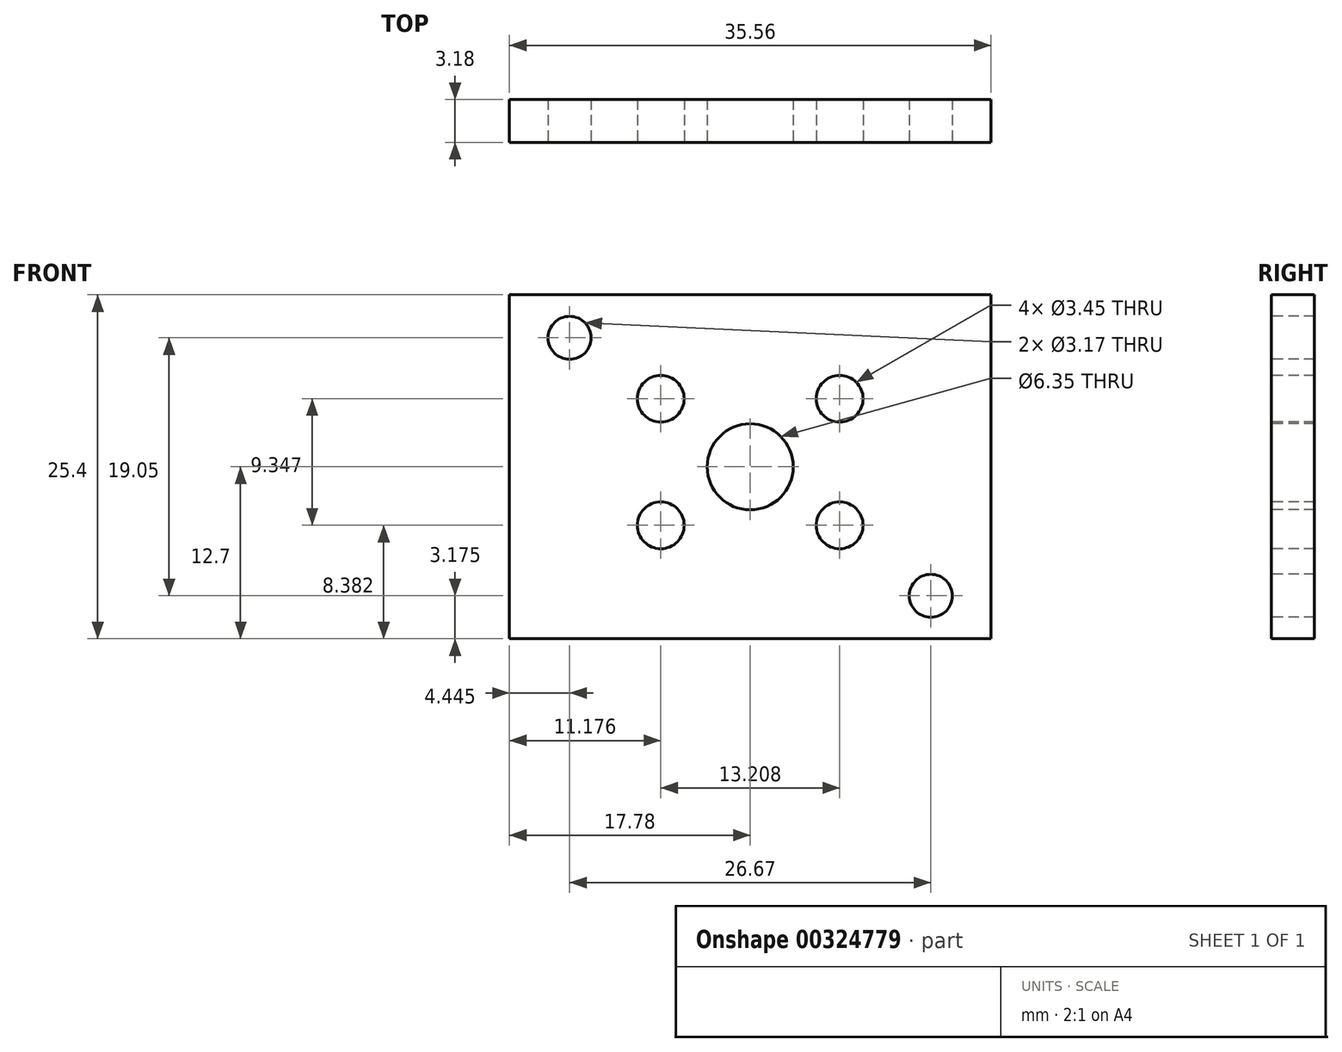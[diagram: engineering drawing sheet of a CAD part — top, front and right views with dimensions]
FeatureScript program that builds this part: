
annotation { "Feature Type Name" : "Feature", "Feature Type Description" : "" }
export const myFeature = defineFeature(function(context is Context, id is Id, definition is map)
    precondition{}
    {
        {
            var Q0;
            Q0=qCreatedBy(makeId("Front.planeOp"),FACE);
            var sketch = newSketch(context, id + "F0", { "sketchPlane" : qUnion([Q0])});
            skLineSegment(sketch, "E0.bottom", {"start": v(17.78, -12.7) * mm, "end": v(-17.78, -12.7) * mm});
            skLineSegment(sketch, "E0.top", {"start": v(17.78, 12.7) * mm, "end": v(-17.78, 12.7) * mm});
            skLineSegment(sketch, "E0.left", {"start": v(17.78, -12.7) * mm, "end": v(17.78, 12.7) * mm});
            skLineSegment(sketch, "E0.right", {"start": v(-17.78, -12.7) * mm, "end": v(-17.78, 12.7) * mm});
            skPoint(sketch, "E0.middle", {"position": v(0, 0) * mm});
            skSolve(sketch);
        }
        {
            var Q0;
            Q0=makeQuery(id+"F0.imprint","IMPRINT",FACE,{"disambiguationData":[TD([[makeQuery(id+"F0.imprint","IMPRINT",EDGE,{"derivedFrom":sQuery(id+"F0.wireOp",EDGE,"E0.bottom")}),-1.0]])]});
            extrude(context, id + "F1", {"entities" : qUnion([Q0]), "depth" : 3.17 * mm, "offsetDistance" : 25.4 * mm});
        }
        {
            var Q0;
            Q0=makeQuery(id+"F1.opExtrude","CAP_FACE",FACE,{"disambiguationData":[OSD([sQuery(id+"F0.wireOp",EDGE,"E0.bottom"),sQuery(id+"F0.wireOp",EDGE,"E0.top"),sQuery(id+"F0.wireOp",EDGE,"E0.left"),sQuery(id+"F0.wireOp",EDGE,"E0.right")])],"isStart":false});
            var sketch = newSketch(context, id + "F2", { "sketchPlane" : qUnion([Q0])});
            skCircle(sketch, "E1", {"center": v(0, 0) * mm, "radius": 3.18 * mm});
            skCircle(sketch, "E2", {"center": v(6.6, 5.03) * mm, "radius": 1.73 * mm});
            skCircle(sketch, "E3", {"center": v(6.6, -4.32) * mm, "radius": 1.73 * mm});
            skCircle(sketch, "E4", {"center": v(-6.6, -4.32) * mm, "radius": 1.73 * mm});
            skCircle(sketch, "E5", {"center": v(-6.6, 5.03) * mm, "radius": 1.73 * mm});
            skSolve(sketch);
        }
        {
            var Q0;
            Q0 = qSketchRegion(id + "F2", true);
            extrude(context, id + "F3", {"entities" : qUnion([Q0]), "operationType" : NewBodyOperationType.REMOVE, "endBound" : BoundingType.THROUGH_ALL, "oppositeDirection" : true, "depth" : 25.4 * mm, "offsetDistance" : 25.4 * mm});
        }
        {
            var Q0;
            Q0=makeQuery(id+"F1.opExtrude","CAP_FACE",FACE,{"disambiguationData":[OSD([sQuery(id+"F0.wireOp",EDGE,"E0.bottom"),sQuery(id+"F0.wireOp",EDGE,"E0.top"),sQuery(id+"F0.wireOp",EDGE,"E0.left"),sQuery(id+"F0.wireOp",EDGE,"E0.right")])],"isStart":false});
            var sketch = newSketch(context, id + "F4", { "sketchPlane" : qUnion([Q0])});
            skLineSegment(sketch, "E6", {"start": v(-17.78, 12.7) * mm, "end": v(17.78, -12.7) * mm, "construction": true});
            skCircle(sketch, "E7", {"center": v(-13.34, 9.53) * mm, "radius": 1.59 * mm});
            skCircle(sketch, "E8", {"center": v(13.34, -9.53) * mm, "radius": 1.59 * mm});
            skSolve(sketch);
        }
        {
            var Q0;
            Q0=makeQuery(id+"F4.imprint","IMPRINT",FACE,{"disambiguationData":[TD([[makeQuery(id+"F4.imprint","IMPRINT",EDGE,{"derivedFrom":sQuery(id+"F4.wireOp",EDGE,"E7")}),1.0]])]});
            var Q1;
            Q1=makeQuery(id+"F4.imprint","IMPRINT",FACE,{"disambiguationData":[TD([[makeQuery(id+"F4.imprint","IMPRINT",EDGE,{"derivedFrom":sQuery(id+"F4.wireOp",EDGE,"E8")}),1.0]])]});
            extrude(context, id + "F5", {"entities" : qUnion([Q0, Q1]), "operationType" : NewBodyOperationType.REMOVE, "endBound" : BoundingType.THROUGH_ALL, "oppositeDirection" : true, "depth" : 25.4 * mm, "offsetDistance" : 25.4 * mm});
        }
    });
